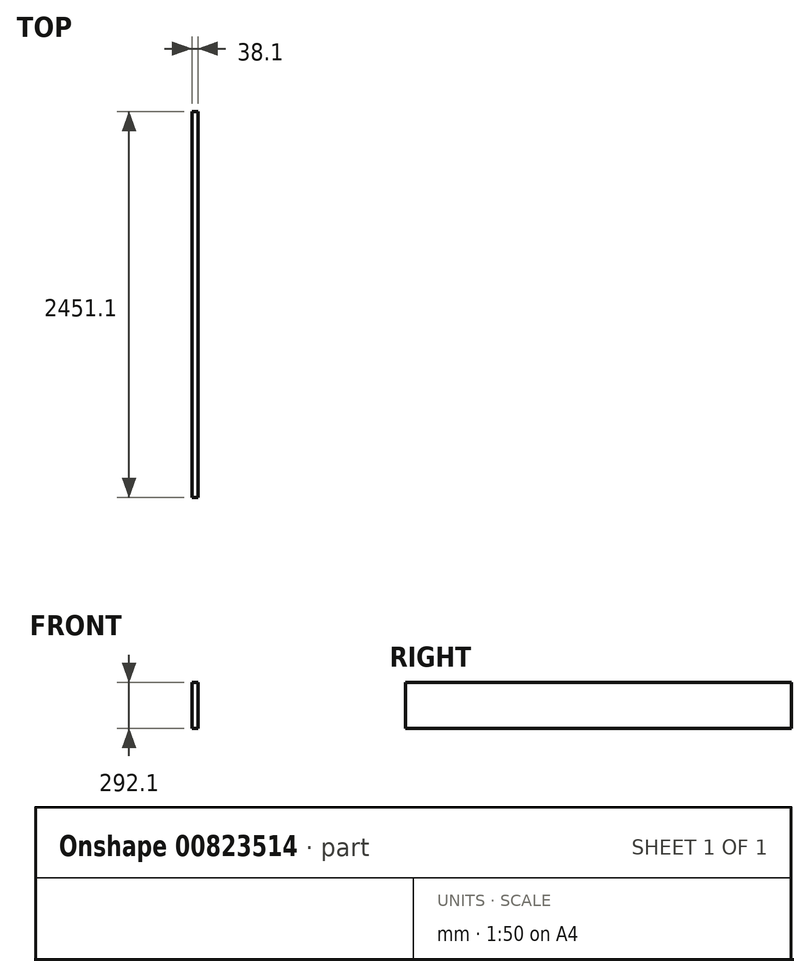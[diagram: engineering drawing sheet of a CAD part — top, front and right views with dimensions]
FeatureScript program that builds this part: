
annotation { "Feature Type Name" : "Feature", "Feature Type Description" : "" }
export const myFeature = defineFeature(function(context is Context, id is Id, definition is map)
    precondition{}
    {
        {
            var Q0;
            Q0=qCreatedBy(makeId("Front.planeOp"),FACE);
            var sketch = newSketch(context, id + "F0", { "sketchPlane" : qUnion([Q0])});
            skLineSegment(sketch, "E0.bottom", {"start": v(0, 0) * mm, "end": v(38.1, 0) * mm});
            skLineSegment(sketch, "E0.top", {"start": v(0, 292.1) * mm, "end": v(38.1, 292.1) * mm});
            skLineSegment(sketch, "E0.left", {"start": v(0, 0) * mm, "end": v(0, 292.1) * mm});
            skLineSegment(sketch, "E0.right", {"start": v(38.1, 0) * mm, "end": v(38.1, 292.1) * mm});
            skSolve(sketch);
        }
        {
            var Q0;
            Q0 = qSketchRegion(id + "F0", true);
            extrude(context, id + "F1", {"entities" : qUnion([Q0]), "depth" : 2451.1 * mm, "offsetDistance" : 25.4 * mm});
        }
    });
